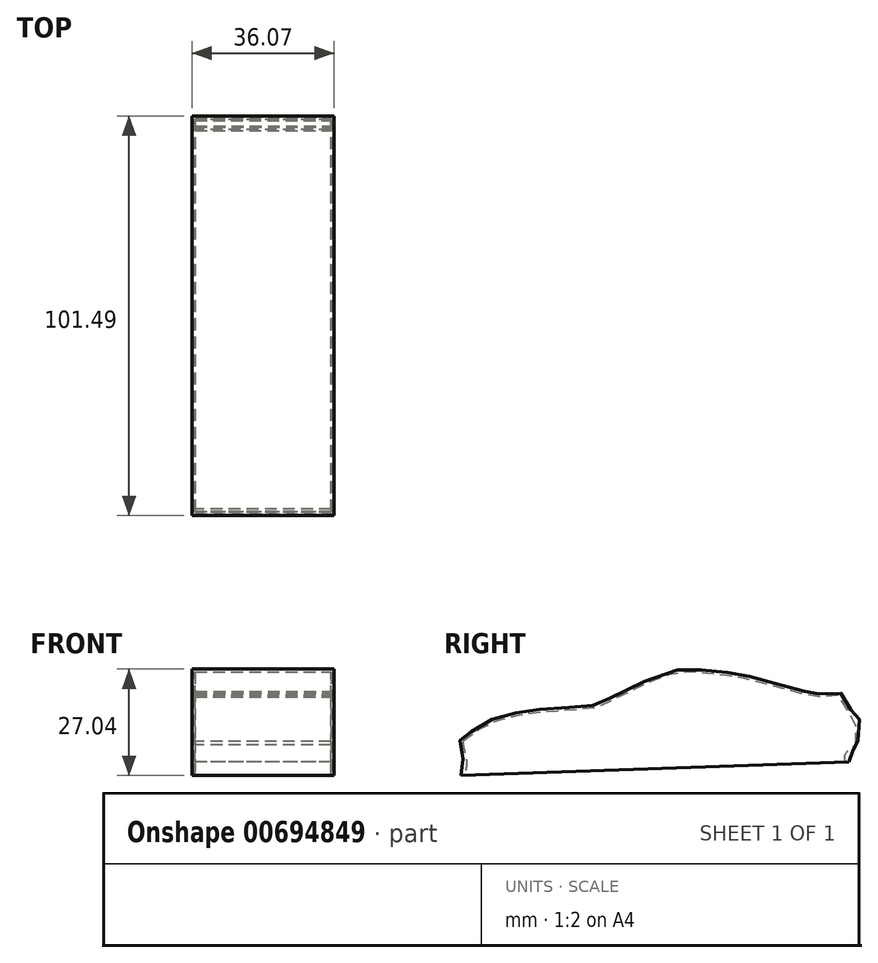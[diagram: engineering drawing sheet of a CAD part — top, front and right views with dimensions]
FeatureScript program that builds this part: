
annotation { "Feature Type Name" : "Feature", "Feature Type Description" : "" }
export const myFeature = defineFeature(function(context is Context, id is Id, definition is map)
    precondition{}
    {
        {
            var Q0;
            Q0=qCreatedBy(makeId("Right.planeOp"),FACE);
            var sketch = newSketch(context, id + "F0", { "sketchPlane" : qUnion([Q0])});
            skLineSegment(sketch, "E0", {"start": v(-62.53, -4.3) * mm, "end": v(36.02, -0.84) * mm});
            skFitSpline(sketch, "E1", {"points": [v(36.02, -0.84) * mm, v(36.02, 1.06) * mm, v(38.54, 3.16) * mm, v(38.33, 4.74) * mm, v(38.54, 10.84) * mm, v(36.86, 12) * mm, v(34.34, 16.41) * mm, v(28.13, 16.41) * mm, v(26.34, 16.62) * mm, v(14.77, 19.78) * mm, v(7.62, 21.46) * mm, v(-1.42, 22.51) * mm, v(-10.15, 21.88) * mm, v(-26.77, 14.3) * mm, v(-29.5, 13.47) * mm, v(-40.13, 12.62) * mm, v(-48.44, 11.57) * mm, v(-56.75, 8.94) * mm, v(-61.8, 5.37) * mm, v(-62.74, 4.53) * mm, v(-61.9, -0.84) * mm, v(-62.53, -4.3) * mm], "startDerivative": vector(-22.36, 69.65) * mm, "endDerivative": vector(-29.53, -78.74) * mm});
            skSolve(sketch);
        }
        {
            var Q0;
            Q0 = qSketchRegion(id + "F0", true);
            extrude(context, id + "F1", {"entities" : qUnion([Q0]), "depth" : 36.07 * mm, "offsetDistance" : 25.4 * mm});
        }
        {
            var Q0;
            Q0=makeQuery(id+"F1.opExtrude","SWEPT_FACE",FACE,{"disambiguationData":[OSD([sQuery(id+"F0.wireOp",EDGE,"E0")])]});
            shell(context, id + "F2", {"entities" : qUnion([Q0]), "thickness" : 0.76 * mm});
        }
    });
